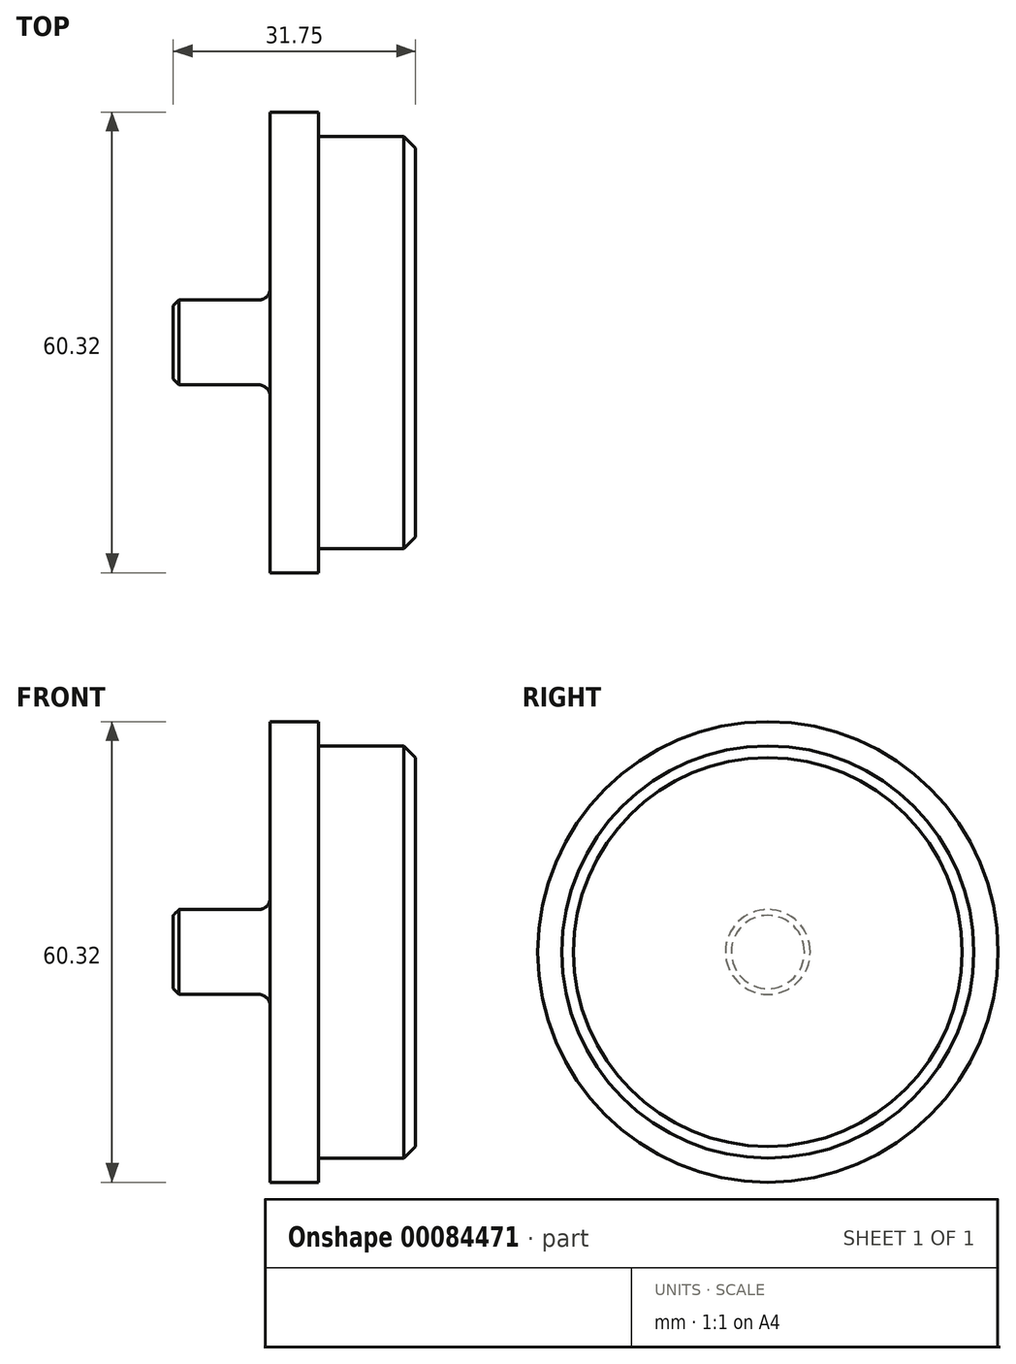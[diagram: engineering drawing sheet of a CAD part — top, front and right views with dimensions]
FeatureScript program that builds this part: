
annotation { "Feature Type Name" : "Feature", "Feature Type Description" : "" }
export const myFeature = defineFeature(function(context is Context, id is Id, definition is map)
    precondition{}
    {
        {
            var Q0;
            Q0=qCreatedBy(makeId("Front.planeOp"),FACE);
            var sketch = newSketch(context, id + "F0", { "sketchPlane" : qUnion([Q0])});
            skLineSegment(sketch, "E0", {"start": v(0, 0) * mm, "end": v(-31.75, 0) * mm});
            skLineSegment(sketch, "E1", {"start": v(0, 0) * mm, "end": v(0, 26.99) * mm});
            skLineSegment(sketch, "E2", {"start": v(0, 26.99) * mm, "end": v(-12.7, 26.99) * mm});
            skLineSegment(sketch, "E3", {"start": v(-12.7, 26.99) * mm, "end": v(-12.7, 30.16) * mm});
            skLineSegment(sketch, "E4", {"start": v(-12.7, 30.16) * mm, "end": v(-19.05, 30.16) * mm});
            skLineSegment(sketch, "E5", {"start": v(-19.05, 30.16) * mm, "end": v(-19.05, 5.56) * mm});
            skLineSegment(sketch, "E6", {"start": v(-19.05, 5.56) * mm, "end": v(-31.75, 5.56) * mm});
            skLineSegment(sketch, "E7", {"start": v(-31.75, 5.56) * mm, "end": v(-31.75, 0) * mm});
            skSolve(sketch);
        }
        {
            var Q0;
            Q0 = qSketchRegion(id + "F0", true);
            var Q1;
            Q1=sQuery(id+"F0.wireOp",EDGE,"E0");
            revolve(context, id + "F1", {"entities" : qUnion([Q0]), "axis" : qUnion([Q1]), "revolveType" : RevolveType.FULL});
        }
        {
            var Q0;
            Q0=makeQuery(id+"F1.opRevolve","SWEPT_EDGE",EDGE,{"disambiguationData":[OSD([sQuery(id+"F0.wireOp",EDGE,"E5"),sQuery(id+"F0.wireOp",EDGE,"E6")])]});
            fillet(context, id + "F2", {"entities" : qUnion([Q0]), "radius" : 1.52 * mm, "allowEdgeOverflow" : false});
        }
        {
            var Q0;
            Q0=makeQuery(id+"F1.opRevolve","SWEPT_EDGE",EDGE,{"disambiguationData":[OSD([sQuery(id+"F0.wireOp",EDGE,"E6"),sQuery(id+"F0.wireOp",EDGE,"E7")])]});
            chamfer(context, id + "F3", {"entities" : qUnion([Q0]), "width" : 0.76 * mm, "tangentPropagation" : true});
        }
        {
            var Q0;
            Q0=makeQuery(id+"F1.opRevolve","SWEPT_EDGE",EDGE,{"disambiguationData":[OSD([sQuery(id+"F0.wireOp",EDGE,"E1"),sQuery(id+"F0.wireOp",EDGE,"E2")])]});
            chamfer(context, id + "F4", {"entities" : qUnion([Q0]), "width" : 1.52 * mm, "tangentPropagation" : true});
        }
    });
